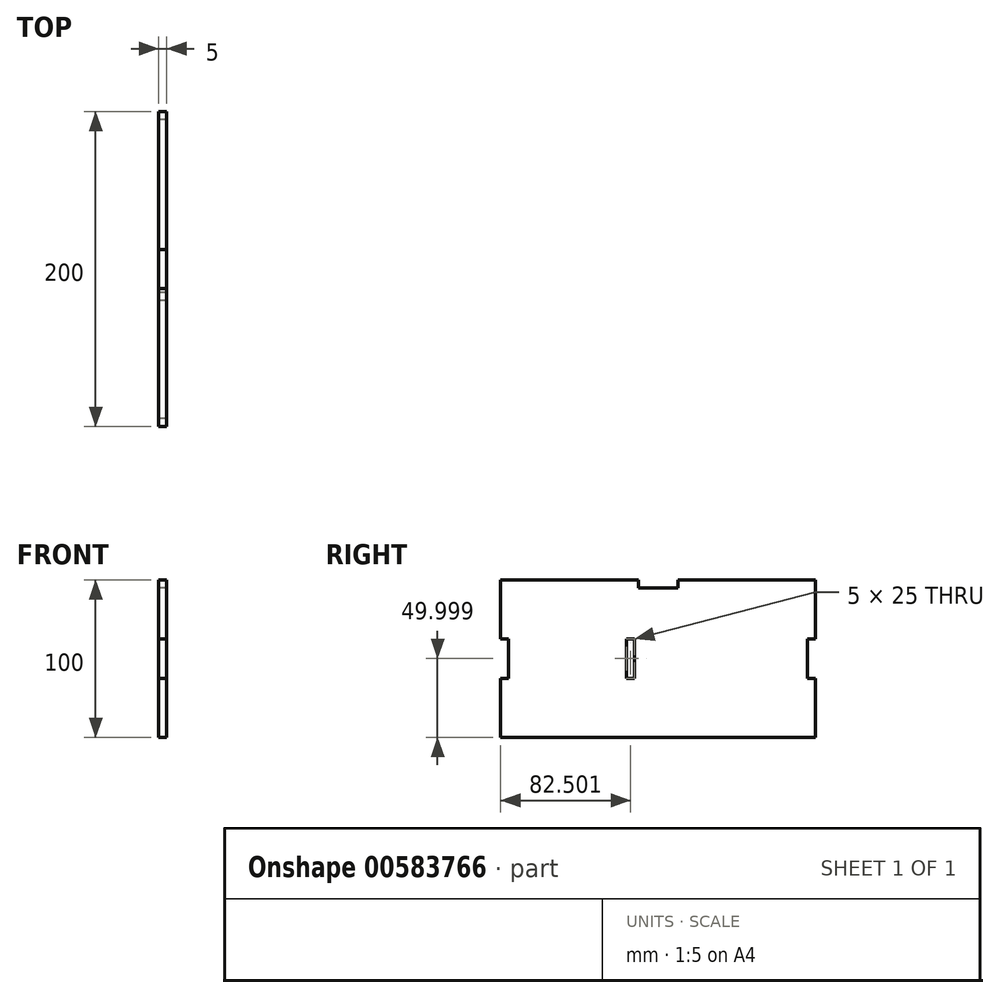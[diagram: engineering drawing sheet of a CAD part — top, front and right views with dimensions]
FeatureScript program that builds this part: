
annotation { "Feature Type Name" : "Feature", "Feature Type Description" : "" }
export const myFeature = defineFeature(function(context is Context, id is Id, definition is map)
    precondition{}
    {
        {
            var Q0;
            Q0=qCreatedBy(makeId("Right.planeOp"),FACE);
            var sketch = newSketch(context, id + "F0", { "sketchPlane" : qUnion([Q0])});
            skLineSegment(sketch, "E0", {"start": v(138.9, 77.3) * mm, "end": v(51.4, 77.3) * mm});
            skLineSegment(sketch, "E1", {"start": v(26.4, 77.3) * mm, "end": v(-61.1, 77.3) * mm});
            skLineSegment(sketch, "E2", {"start": v(51.4, 77.3) * mm, "end": v(51.4, 72.3) * mm});
            skLineSegment(sketch, "E3", {"start": v(51.4, 72.3) * mm, "end": v(26.4, 72.3) * mm});
            skLineSegment(sketch, "E4", {"start": v(26.4, 72.3) * mm, "end": v(26.4, 77.3) * mm});
            skLineSegment(sketch, "E5", {"start": v(138.9, -22.7) * mm, "end": v(138.9, 77.3) * mm});
            skLineSegment(sketch, "E6", {"start": v(-61.1, 77.3) * mm, "end": v(-61.1, 39.8) * mm});
            skLineSegment(sketch, "E7", {"start": v(-61.1, 39.8) * mm, "end": v(-56.1, 39.8) * mm});
            skLineSegment(sketch, "E8", {"start": v(-56.1, 39.8) * mm, "end": v(-56.1, 14.8) * mm});
            skLineSegment(sketch, "E9", {"start": v(-56.1, 14.8) * mm, "end": v(-61.1, 14.8) * mm});
            skLineSegment(sketch, "E10", {"start": v(-61.1, 14.8) * mm, "end": v(-61.1, -22.7) * mm});
            skLineSegment(sketch, "E11", {"start": v(18.9, 39.8) * mm, "end": v(18.9, 14.8) * mm});
            skLineSegment(sketch, "E12", {"start": v(18.9, 39.8) * mm, "end": v(23.9, 39.8) * mm});
            skLineSegment(sketch, "E13", {"start": v(23.9, 39.8) * mm, "end": v(23.9, 14.8) * mm});
            skLineSegment(sketch, "E14", {"start": v(23.9, 14.8) * mm, "end": v(18.9, 14.8) * mm});
            skPoint(sketch, "E15.middle", {"position": v(-21.7, 27.3) * mm});
            skPoint(sketch, "E15.middle.positionSnap0", {"position": v(23.9, 27.3) * mm});
            skPoint(sketch, "E15.centerSnap0", {"position": v(23.9, 27.3) * mm});
            skLineSegment(sketch, "E16", {"start": v(138.9, 39.8) * mm, "end": v(133.9, 39.8) * mm});
            skLineSegment(sketch, "E17", {"start": v(133.9, 39.8) * mm, "end": v(133.9, 14.8) * mm});
            skLineSegment(sketch, "E18", {"start": v(133.9, 14.8) * mm, "end": v(138.9, 14.8) * mm});
            skLineSegment(sketch, "E19", {"start": v(-61.1, -22.7) * mm, "end": v(138.9, -22.7) * mm});
            skSolve(sketch);
        }
        {
            var Q0;
            Q0=makeQuery(id+"F0.imprint","IMPRINT",FACE,{"disambiguationData":[TD([[makeQuery(id+"F0.imprint","IMPRINT",EDGE,{"derivedFrom":sQuery(id+"F0.wireOp",EDGE,"GOybfPKA-ABaV-DC2s-Gll3-hCjfb0mqv9ub")}),1.0]])]});
            var Q1;
            {var subQ1=sQuery(id+"F0.wireOp",EDGE,"E0");Q1=makeQuery(id+"F0.imprint","IMPRINT",FACE,{"disambiguationData":[TD([[makeQuery(id+"F0.imprint","IMPRINT",EDGE,{"derivedFrom":subQ1}),1.0]])]});}
            extrude(context, id + "F1", {"entities" : qUnion([Q0, Q1]), "depth" : 5 * mm, "offsetDistance" : 25 * mm});
        }
    });
